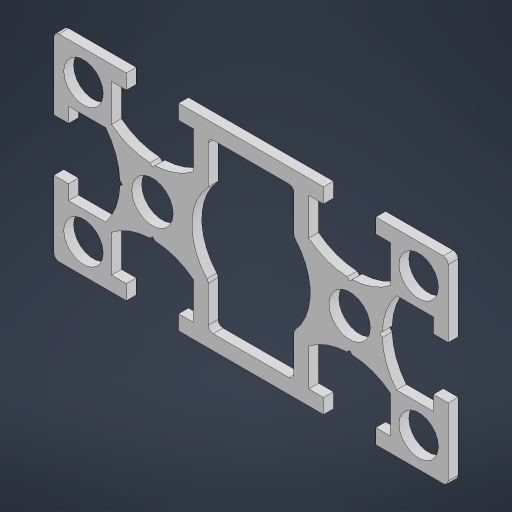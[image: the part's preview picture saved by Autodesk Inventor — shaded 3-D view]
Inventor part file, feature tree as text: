
AUTODESK INVENTOR PART (.ipt)
format: ipt  version: 2024 (Build 280153000, 153)  size: 323,072 bytes
history: native  units: mm
features: other x1, extrude x1, sketch x1
ambient origin geometry x8: Origin, YZ Plane, XZ Plane, XY Plane, X Axis, Y Axis, Z Axis, Center Point
bodies: Body1 (feature_tree)
feature tree (3):
  other  "솔리드1"
  extrude  "돌출1"  Depth=40.0mm
  sketch  "스케치1"
